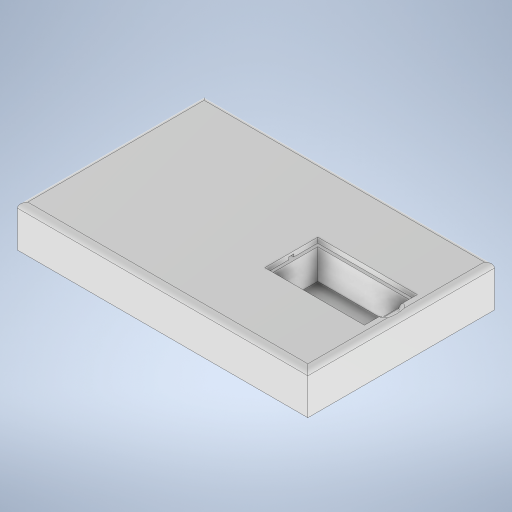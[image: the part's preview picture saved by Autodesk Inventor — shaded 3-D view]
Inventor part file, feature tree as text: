
AUTODESK INVENTOR PART (.ipt)
format: ipt  version: 2023 (Build 270158000, 158)  size: 338,944 bytes
history: native  units: in
note: dims shown in document units (in); Inventor stores cm internally (conversion verified against a paired STEP export)
features: extrude x7, sketch x3, fillet x2, shell x1
ambient origin geometry x8: Origin, YZ Plane, XZ Plane, XY Plane, X Axis, Y Axis, Z Axis, Center Point
bodies: Body1 (feature_tree)
feature tree (13):
  extrude  "Extrusion4"  Depth=4.5in
  extrude  "Extrusion7"  Depth=2.4in
  extrude  "Extrusion8"  Depth=1.125in
  fillet  "Fillet3"  Radius=2.25in
  extrude  "Extrusion11"  Depth=0.075in
  extrude  "Extrusion12"  Depth=0.075in
  fillet  "Fillet4"  Radius=1.6125in
  extrude  "Extrusion13"  Depth=0.25in
  shell  "Shell4"  Thickness=0.125in
  extrude  "Extrusion14"  Depth=0.25in TaperAngle=0.0deg
  sketch  "Sketch1"  dims[d0=7.0in d1=4.5in]
  sketch  "Sketch6"  dims[d32=1.0in d33=0.0in d34=2.4in]
  sketch  "Sketch7"  dims[d35=1.275in d36=1.125in d37=2.25in d38=0.075in d39=0.075in d41=1.6125in d42=0.25in d62=0.125in d63=0.0in d64=0.85in d65=0.0in d75=0.125in d82=1.6125in d83=0.375in d84=0.25in d85=0.5625in d86=1.0in d87=0.0in d88=0.0665in d89=0.0in d90=0.1in d91=0.0625in d92=0.0625in d93=0.0625in d94=0.1in d95=0.0in d96=0.2in d97=0.155in d98=0.155in d99=0.155in d100=0.155in d101=0.155in d102=0.155in d103=0.1in d104=0.1in d105=0.1in d106=0.1in d107=0.1in d108=0.1in d109=0.1in d110=0.1in d111=0.1in d112=0.1in d113=3.5in d114=3.5in d115=0.25in d116=0.0in]
